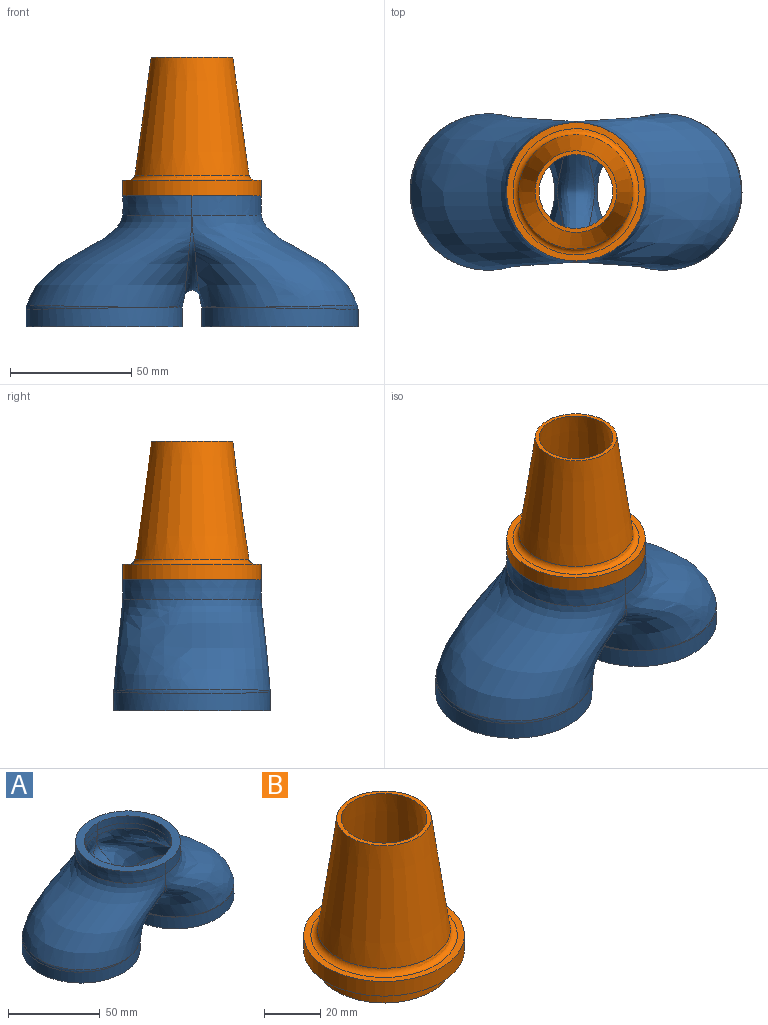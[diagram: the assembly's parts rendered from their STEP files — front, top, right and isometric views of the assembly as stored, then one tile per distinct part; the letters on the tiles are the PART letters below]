
ASSEMBLY  parts=2 mates=1
PART A: 27 faces, bbox 146.6x74.1x63.5 mm
  f0: offset ~106.57x73.98mm, area 5660.1mm2, adj f1,f2,f5,f8,f9,f10
  f1: offset ~106.57x73.98mm, area 5659.7mm2, adj f0,f3,f4,f6,f7,f10
  f2: extruded ~47.63x23.81mm, area 253.3mm2, adj f0,f3,f11
  f3: extruded ~47.63x23.81mm, area 253.2mm2, adj f1,f2,f12
  f4: cylinder r=27.5mm len=55mm, axis (0,0,1), area 1318.8mm2, adj f1,f6,f7,f19
  f5: cylinder r=27.5mm len=55mm, axis (0,0,1), area 1313mm2, adj f0,f8,f9,f21
  f6: bspline ~46.11x12.57mm, area 0mm2, adj f1,f4
  f7: bspline ~55.01x41.93mm, area 8.3mm2, adj f1,f4
  f8: bspline ~46.11x12.57mm, area 0mm2, adj f0,f5
  f9: bspline ~55.01x41.93mm, area 8.3mm2, adj f0,f5
  f10: bspline ~48.58x31.33mm, area 0mm2, adj f0,f1
  f11: extruded ~47.63x23.81mm, area 356.3mm2, adj f2,f12,f17
  f12: extruded ~47.63x23.81mm, area 356.3mm2, adj f3,f11,f17
  f13: bspline ~97.06x64.46mm, area 6472.1mm2, adj f15,f20,f24,f25,f26
  f14: bspline ~97.06x64.46mm, area 6472.2mm2, adj f16,f18,f22,f23,f26
  f15: extruded ~57.15x28.58mm, area 712.7mm2, adj f13,f16,f17
  f16: extruded ~57.15x28.58mm, area 712.7mm2, adj f14,f15,f17
  f17: plane 57.15x57.15mm, normal (0,0,1), area 783.7mm2, adj f11,f12,f15,f16
  f18: cylinder r=32.26mm len=64.53mm, axis (0,0,1), area 1532.4mm2, adj f14,f19,f22,f23
  f19: plane 64.53x64.53mm, normal (0,0,-1), area 894.2mm2, adj f4,f18
  f20: cylinder r=32.26mm len=64.53mm, axis (0,0,1), area 1532.3mm2, adj f13,f21,f24,f25
  f21: plane 64.53x64.53mm, normal (0,0,-1), area 894.2mm2, adj f5,f20
  f22: bspline ~54.12x14.72mm, area 7.1mm2, adj f14,f18
  f23: bspline ~64.52x48.52mm, area 139.9mm2, adj f14,f18
  f24: bspline ~54.12x14.72mm, area 0mm2, adj f13,f20
  f25: bspline ~64.52x48.52mm, area 139.9mm2, adj f13,f20
  f26: bspline ~58.05x33.17mm, area 0mm2, adj f13,f14
PART B: 10 faces, bbox 60.2x60.2x63.5 mm
  f0: cylinder r=22.23mm len=44.45mm, axis (0,0,-1), area 1773.5mm2, adj f2,f8
  f1: cylinder r=23.81mm len=47.63mm, axis (0,0,-1), area 950.1mm2, adj f2,f5
  f2: plane 47.63x47.63mm, normal (0,0,-1), area 229.6mm2, adj f0,f1
  f3: cylinder r=28.57mm len=57.15mm, axis (0,0,-1), area 1140.1mm2, adj f4,f5
  f4: plane 57.15x57.15mm, normal (0,0,1), area 437.1mm2, adj f3,f9
  f5: plane 57.15x57.15mm, normal (0,0,-1), area 783.8mm2, adj f1,f3
  f6: cone r=23.81mm half-angle=7.8deg, axis (0,0,-1), area 6217.6mm2, adj f7,f9
  f7: plane 33.66x33.66mm, normal (0,0,1), area 159.9mm2, adj f6,f8
  f8: cone r=22.23mm half-angle=7.8deg, axis (0,0,-1), area 6035.4mm2, adj f0,f7
  f9: torus R=26.03mm, axis (0,0,1), area 560.7mm2, adj f4,f6
PLACE A t=(5.32,-5.57,36.93)mm
PLACE B t=(41.57,-5.57,76.61)mm
MATE planar A.f17 <-> B.f6  axis (0,0,1) through (41.57,-5.57,82.96)mm
